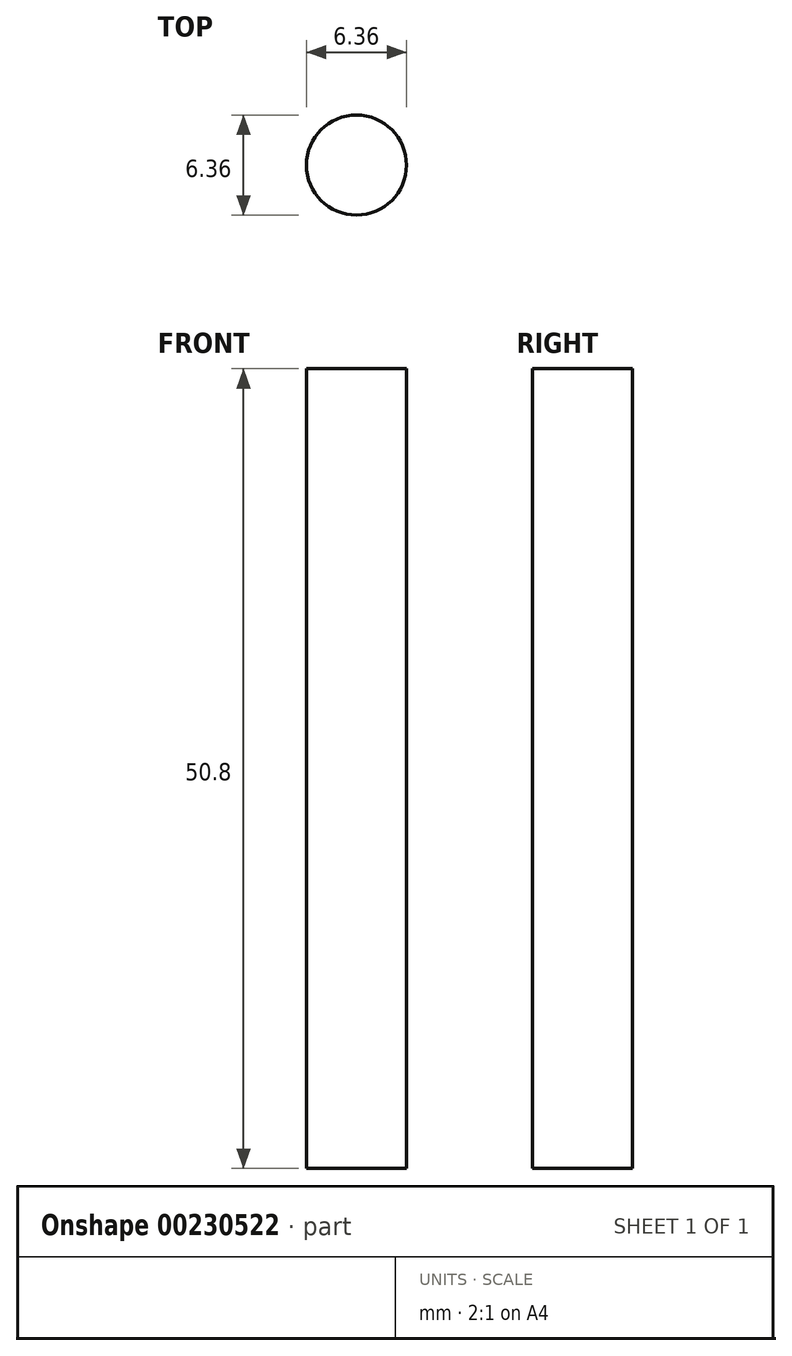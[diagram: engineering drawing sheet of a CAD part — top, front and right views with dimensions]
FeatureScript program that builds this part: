
annotation { "Feature Type Name" : "Feature", "Feature Type Description" : "" }
export const myFeature = defineFeature(function(context is Context, id is Id, definition is map)
    precondition{}
    {
        {
            var Q0;
            Q0=qCreatedBy(makeId("Top.planeOp"),FACE);
            var sketch = newSketch(context, id + "F0", { "sketchPlane" : qUnion([Q0])});
            skCircle(sketch, "E0", {"center": v(0, 0) * mm, "radius": 3.17 * mm});
            skSolve(sketch);
        }
        {
            var Q0;
            Q0=sQuery(id+"F0.wireOp",EDGE,"E0");
            extrude(context, id + "F1", {"bodyType" : ToolBodyType.SURFACE, "surfaceEntities" : qUnion([Q0]), "depth" : 50.8 * mm});
        }
    });
